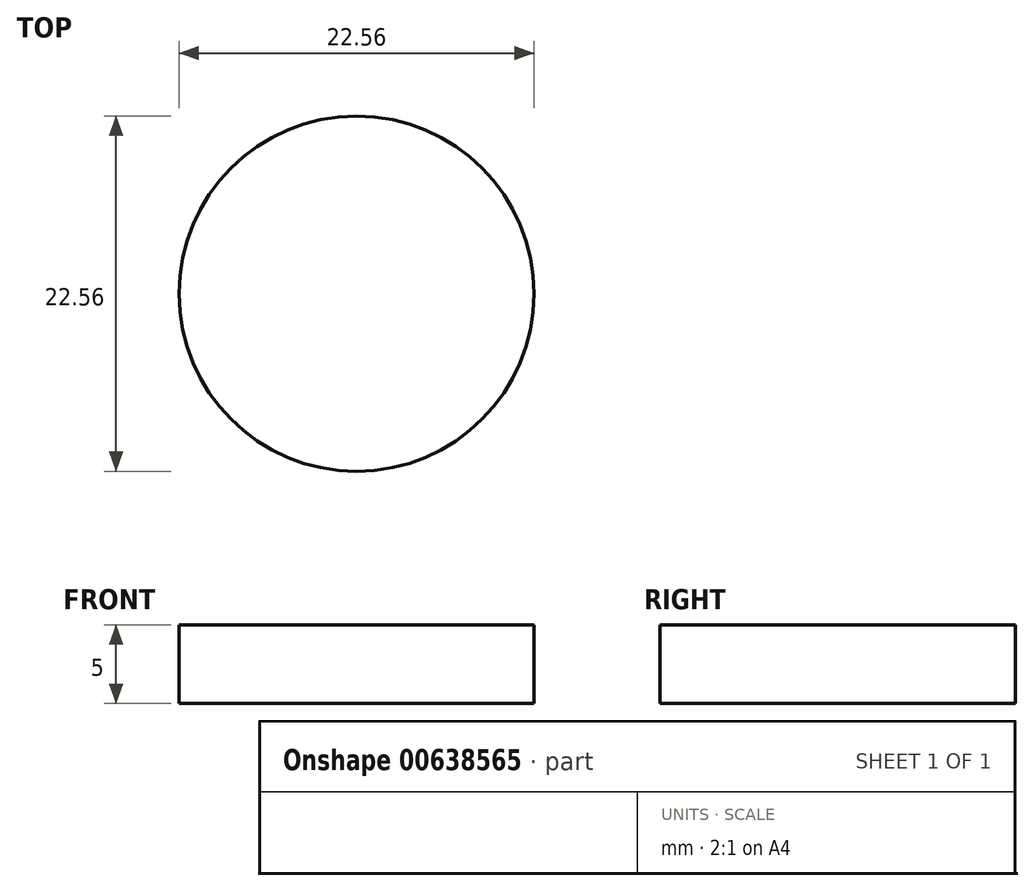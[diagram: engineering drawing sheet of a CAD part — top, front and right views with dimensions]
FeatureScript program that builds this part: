
annotation { "Feature Type Name" : "Feature", "Feature Type Description" : "" }
export const myFeature = defineFeature(function(context is Context, id is Id, definition is map)
    precondition{}
    {
        {
            var Q0;
            Q0=qCreatedBy(makeId("Top.planeOp"),FACE);
            var sketch = newSketch(context, id + "F0", { "sketchPlane" : qUnion([Q0])});
            skCircle(sketch, "E0", {"center": v(0, 0) * mm, "radius": 11.28 * mm});
            skSolve(sketch);
        }
        {
            var Q0;
            Q0 = qSketchRegion(id + "F0", true);
            extrude(context, id + "F1", {"entities" : qUnion([Q0]), "depth" : 5 * mm, "offsetDistance" : 25 * mm});
        }
    });
